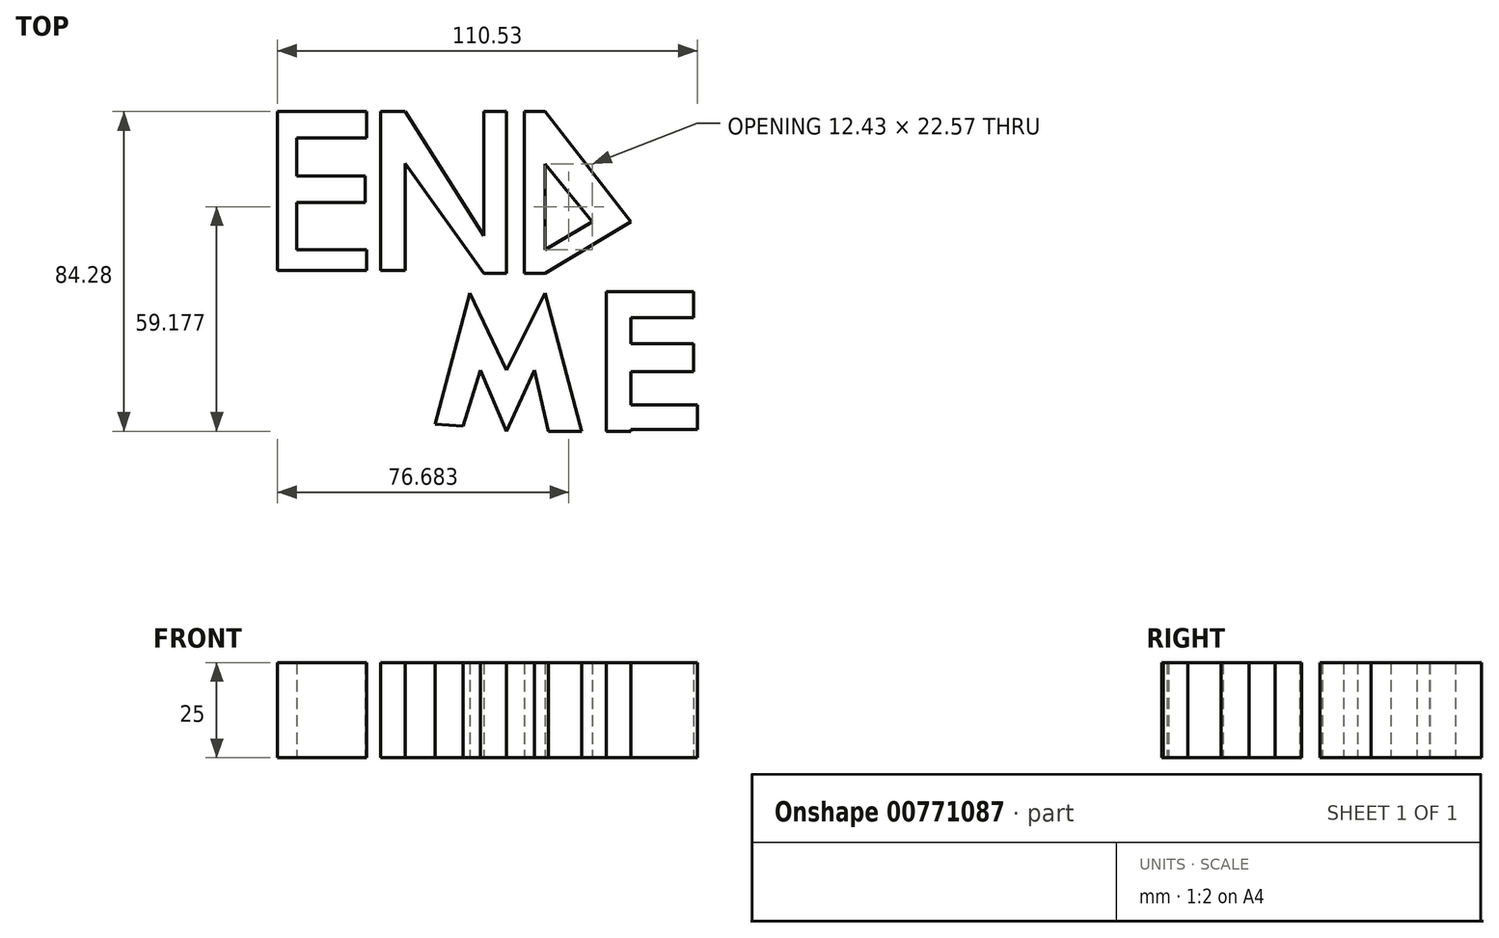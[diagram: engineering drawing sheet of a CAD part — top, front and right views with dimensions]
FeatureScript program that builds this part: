
annotation { "Feature Type Name" : "Feature", "Feature Type Description" : "" }
export const myFeature = defineFeature(function(context is Context, id is Id, definition is map)
    precondition{}
    {
        {
            var Q0;
            Q0=qCreatedBy(makeId("Top.planeOp"),FACE);
            var sketch = newSketch(context, id + "F0", { "sketchPlane" : qUnion([Q0])});
            skLineSegment(sketch, "E0.bottom", {"start": v(-63.19, 29.1) * mm, "end": v(-58.12, 29.1) * mm});
            skLineSegment(sketch, "E0.top", {"start": v(-63.19, -12.8) * mm, "end": v(-58.12, -12.8) * mm});
            skLineSegment(sketch, "E0.left", {"start": v(-63.19, 29.1) * mm, "end": v(-63.19, -12.8) * mm});
            skLineSegment(sketch, "E0.right", {"start": v(-58.12, 29.1) * mm, "end": v(-58.12, -12.8) * mm});
            skLineSegment(sketch, "E1.bottom", {"start": v(-39.7, 29.1) * mm, "end": v(-58.12, 29.1) * mm});
            skLineSegment(sketch, "E1.top", {"start": v(-39.7, 22.2) * mm, "end": v(-58.12, 22.2) * mm});
            skLineSegment(sketch, "E1.left", {"start": v(-39.7, 29.1) * mm, "end": v(-39.7, 22.2) * mm});
            skLineSegment(sketch, "E1.right", {"start": v(-58.12, 29.1) * mm, "end": v(-58.12, 22.2) * mm});
            skLineSegment(sketch, "E2.bottom", {"start": v(-39.7, -12.8) * mm, "end": v(-58.12, -12.8) * mm});
            skLineSegment(sketch, "E2.top", {"start": v(-39.7, -7.28) * mm, "end": v(-58.12, -7.28) * mm});
            skLineSegment(sketch, "E2.left", {"start": v(-39.7, -12.8) * mm, "end": v(-39.7, -7.28) * mm});
            skLineSegment(sketch, "E2.right", {"start": v(-58.12, -12.8) * mm, "end": v(-58.12, -7.28) * mm});
            skLineSegment(sketch, "E3.bottom", {"start": v(-58.12, 12.07) * mm, "end": v(-40.16, 12.07) * mm});
            skLineSegment(sketch, "E3.top", {"start": v(-58.12, 5.16) * mm, "end": v(-40.16, 5.16) * mm});
            skLineSegment(sketch, "E3.left", {"start": v(-58.12, 12.07) * mm, "end": v(-58.12, 5.16) * mm});
            skLineSegment(sketch, "E3.right", {"start": v(-40.16, 12.07) * mm, "end": v(-40.16, 5.16) * mm});
            skLineSegment(sketch, "E4.bottom", {"start": v(-36.01, 29.1) * mm, "end": v(-29.57, 29.1) * mm});
            skLineSegment(sketch, "E4.top", {"start": v(-36.01, -12.8) * mm, "end": v(-29.57, -12.8) * mm});
            skLineSegment(sketch, "E4.left", {"start": v(-36.01, 29.1) * mm, "end": v(-36.01, -12.8) * mm});
            skLineSegment(sketch, "E4.right", {"start": v(-29.57, 29.1) * mm, "end": v(-29.57, -12.8) * mm});
            skLineSegment(sketch, "E5", {"start": v(-29.57, 29.1) * mm, "end": v(-36.01, 24.5) * mm});
            skLineSegment(sketch, "E6", {"start": v(-36.01, 24.5) * mm, "end": v(-8.85, -13.53) * mm});
            skLineSegment(sketch, "E7", {"start": v(-8.85, -13.53) * mm, "end": v(-4.54, -10.45) * mm});
            skLineSegment(sketch, "E8", {"start": v(-4.54, -10.45) * mm, "end": v(-29.57, 29.1) * mm});
            skLineSegment(sketch, "E9.bottom", {"start": v(-8.85, -13.53) * mm, "end": v(-2.86, -13.53) * mm});
            skLineSegment(sketch, "E9.top", {"start": v(-8.85, 29.1) * mm, "end": v(-2.86, 29.1) * mm});
            skLineSegment(sketch, "E9.left", {"start": v(-8.85, -13.53) * mm, "end": v(-8.85, 29.1) * mm});
            skLineSegment(sketch, "E9.right", {"start": v(-2.86, -13.53) * mm, "end": v(-2.86, 29.1) * mm});
            skLineSegment(sketch, "E10.bottom", {"start": v(1.75, 29.1) * mm, "end": v(7.28, 29.1) * mm});
            skLineSegment(sketch, "E10.top", {"start": v(1.75, -13.53) * mm, "end": v(7.28, -13.53) * mm});
            skLineSegment(sketch, "E10.left", {"start": v(1.75, 29.1) * mm, "end": v(1.75, -13.53) * mm});
            skLineSegment(sketch, "E10.right", {"start": v(7.28, 15.29) * mm, "end": v(7.28, -7.28) * mm});
            skLineSegment(sketch, "E11", {"start": v(7.28, 29.1) * mm, "end": v(29.84, 0) * mm});
            skLineSegment(sketch, "E12", {"start": v(29.84, 0) * mm, "end": v(7.28, -13.53) * mm});
            skLineSegment(sketch, "E13", {"start": v(7.28, 15.29) * mm, "end": v(19.7, 0) * mm});
            skLineSegment(sketch, "E14", {"start": v(19.7, 0) * mm, "end": v(7.28, -7.28) * mm});
            skLineSegment(sketch, "E15", {"start": v(-21.74, -53.33) * mm, "end": v(-12.53, -18.79) * mm});
            skLineSegment(sketch, "E16", {"start": v(-12.53, -18.79) * mm, "end": v(-2.86, -39.05) * mm});
            skLineSegment(sketch, "E17", {"start": v(-2.86, -39.05) * mm, "end": v(7.28, -18.79) * mm});
            skLineSegment(sketch, "E18", {"start": v(7.28, -18.79) * mm, "end": v(16.95, -55.17) * mm});
            skLineSegment(sketch, "E19", {"start": v(16.95, -55.17) * mm, "end": v(8.2, -55.17) * mm});
            skLineSegment(sketch, "E20", {"start": v(8.2, -55.17) * mm, "end": v(4.51, -39.05) * mm});
            skLineSegment(sketch, "E21", {"start": v(4.51, -39.05) * mm, "end": v(-2.86, -55.17) * mm});
            skLineSegment(sketch, "E22", {"start": v(-2.86, -55.17) * mm, "end": v(-9.76, -39.05) * mm});
            skLineSegment(sketch, "E23", {"start": v(-9.76, -39.05) * mm, "end": v(-14.37, -53.79) * mm});
            skLineSegment(sketch, "E24", {"start": v(-14.37, -53.79) * mm, "end": v(-21.74, -53.33) * mm});
            skLineSegment(sketch, "E25.bottom", {"start": v(23.4, -18.33) * mm, "end": v(29.84, -18.33) * mm});
            skLineSegment(sketch, "E25.top", {"start": v(23.4, -55.17) * mm, "end": v(29.84, -55.17) * mm});
            skLineSegment(sketch, "E25.left", {"start": v(23.4, -18.33) * mm, "end": v(23.4, -55.17) * mm});
            skLineSegment(sketch, "E25.right", {"start": v(29.84, -18.33) * mm, "end": v(29.84, -55.17) * mm});
            skLineSegment(sketch, "E26.bottom", {"start": v(46.42, -18.33) * mm, "end": v(29.84, -18.33) * mm});
            skLineSegment(sketch, "E26.top", {"start": v(46.42, -25.24) * mm, "end": v(29.84, -25.24) * mm});
            skLineSegment(sketch, "E26.left", {"start": v(46.42, -18.33) * mm, "end": v(46.42, -25.24) * mm});
            skLineSegment(sketch, "E26.right", {"start": v(29.84, -18.33) * mm, "end": v(29.84, -25.24) * mm});
            skLineSegment(sketch, "E27.bottom", {"start": v(47.34, -54.71) * mm, "end": v(29.84, -54.71) * mm});
            skLineSegment(sketch, "E27.top", {"start": v(47.34, -48.26) * mm, "end": v(29.84, -48.26) * mm});
            skLineSegment(sketch, "E27.left", {"start": v(47.34, -54.71) * mm, "end": v(47.34, -48.26) * mm});
            skLineSegment(sketch, "E27.right", {"start": v(29.84, -54.71) * mm, "end": v(29.84, -48.26) * mm});
            skLineSegment(sketch, "E28.bottom", {"start": v(46.42, -32.14) * mm, "end": v(29.84, -32.14) * mm});
            skLineSegment(sketch, "E28.top", {"start": v(46.42, -39.51) * mm, "end": v(29.84, -39.51) * mm});
            skLineSegment(sketch, "E28.left", {"start": v(46.42, -32.14) * mm, "end": v(46.42, -39.51) * mm});
            skLineSegment(sketch, "E28.right", {"start": v(29.84, -32.14) * mm, "end": v(29.84, -39.51) * mm});
            skSolve(sketch);
        }
        {
            var Q0;
            Q0 = qSketchRegion(id + "F0", true);
            extrude(context, id + "F1", {"entities" : qUnion([Q0]), "depth" : 25 * mm, "offsetDistance" : 25 * mm});
        }
    });
